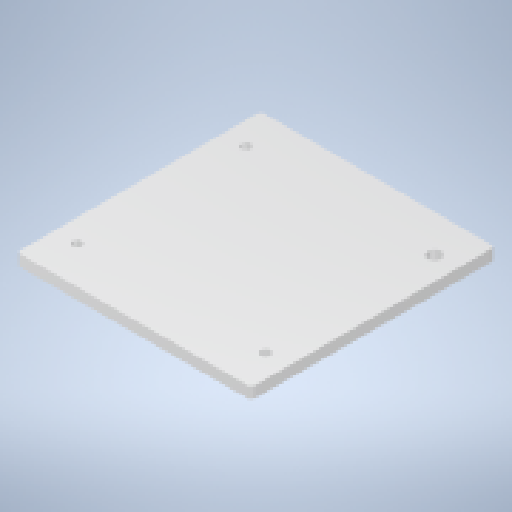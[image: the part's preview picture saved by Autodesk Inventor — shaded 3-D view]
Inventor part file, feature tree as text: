
AUTODESK INVENTOR PART (.ipt)
format: ipt  version: 2023.2 (Build 272271000, 271)  size: 236,032 bytes
history: native  units: mm
features: extrude x1, fillet x1, sketch x1
ambient origin geometry x8: Origin, YZ Plane, XZ Plane, XY Plane, X Axis, Y Axis, Z Axis, Center Point
bodies: Solid1 (feature_tree)
feature tree (3):
  extrude  "Extrusion1"  Depth=130.0mm
  fillet  "Fillet1"  Radius=5.1mm
  sketch  "Sketch1"  dims[d0=125.0mm d1=130.0mm d4=5.1mm d5=5.1mm d6=5.1mm d7=7.1mm d8=6.0mm d9=0.0mm d10=2.0mm d11=100.4mm d12=20.0mm d13=20.0mm d14=20.0mm d15=20.0mm]
